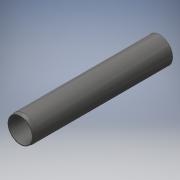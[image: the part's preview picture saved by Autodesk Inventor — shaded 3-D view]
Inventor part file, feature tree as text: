
AUTODESK INVENTOR PART (.ipt)
format: ipt  version: 2016 (Build 200138000, 138)  size: 101,376 bytes
history: native  units: mm
features: sketch x2, extrude x1, chamfer x1
ambient origin geometry x8: Origin, YZ Plane, XZ Plane, XY Plane, X Axis, Y Axis, Z Axis, Center Point
bodies: Solid1 (feature_tree)
feature tree (4):
  extrude  "Extrusion1"  Depth=400.0mm
  sketch  "Sketch2"  dims[d8=1.75mm d9=10.0mm d10=45.0deg]
  chamfer  "Chamfer2"  Distance=400.0mm
  sketch  "Sketch1"  dims[d0=75.0mm d1=3.5mm d2=400.0mm d3=0.0mm]
